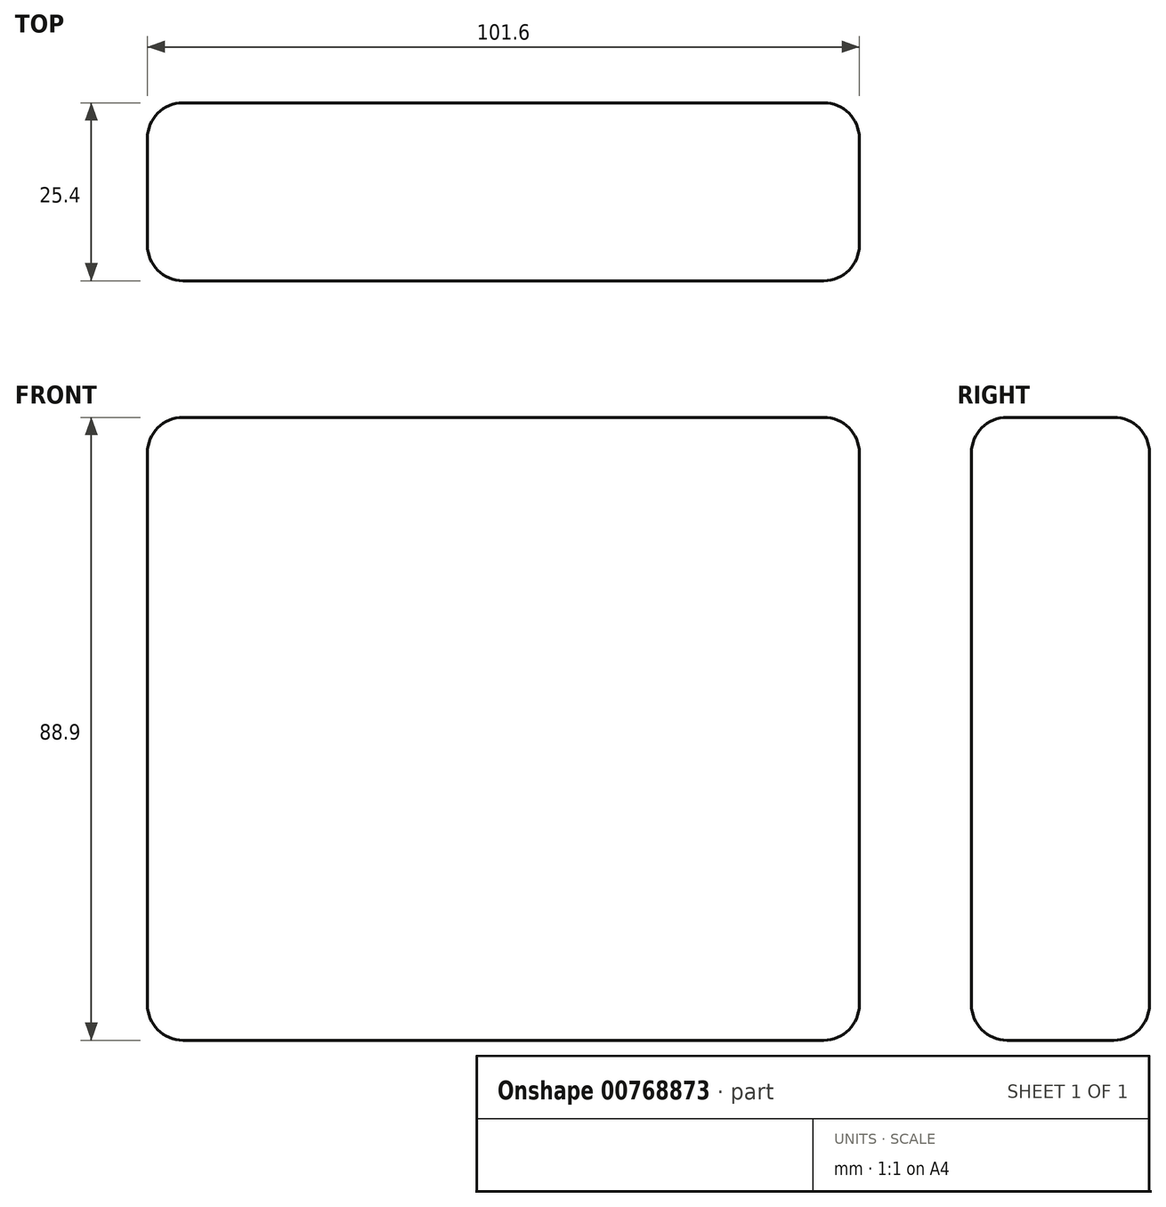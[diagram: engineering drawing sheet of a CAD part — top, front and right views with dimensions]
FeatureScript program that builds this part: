
annotation { "Feature Type Name" : "Feature", "Feature Type Description" : "" }
export const myFeature = defineFeature(function(context is Context, id is Id, definition is map)
    precondition{}
    {
        {
            var Q0;
            Q0=qCreatedBy(makeId("Front.planeOp"),FACE);
            var sketch = newSketch(context, id + "F0", { "sketchPlane" : qUnion([Q0])});
            skLineSegment(sketch, "E0.bottom", {"start": v(-50.8, -44.45) * mm, "end": v(50.8, -44.45) * mm});
            skLineSegment(sketch, "E0.top", {"start": v(-50.8, 44.45) * mm, "end": v(50.8, 44.45) * mm});
            skLineSegment(sketch, "E0.left", {"start": v(-50.8, -44.45) * mm, "end": v(-50.8, 44.45) * mm});
            skLineSegment(sketch, "E0.right", {"start": v(50.8, -44.45) * mm, "end": v(50.8, 44.45) * mm});
            skPoint(sketch, "E0.middle", {"position": v(0, 0) * mm});
            skSolve(sketch);
        }
        {
            var Q0;
            Q0 = qSketchRegion(id + "F0", true);
            extrude(context, id + "F1", {"entities" : qUnion([Q0]), "depth" : 25.4 * mm, "offsetDistance" : 25.4 * mm});
        }
        {
            var Q0;
            Q0=makeQuery(id+"F1.opExtrude","CAP_EDGE",EDGE,{"disambiguationData":[OSD([sQuery(id+"F0.wireOp",EDGE,"E0.top")])],"isStart":false});
            var Q1;
            Q1=makeQuery(id+"F1.opExtrude","CAP_EDGE",EDGE,{"disambiguationData":[OSD([sQuery(id+"F0.wireOp",EDGE,"E0.right")])],"isStart":false});
            var Q2;
            Q2=makeQuery(id+"F1.opExtrude","CAP_EDGE",EDGE,{"disambiguationData":[OSD([sQuery(id+"F0.wireOp",EDGE,"E0.bottom")])],"isStart":false});
            var Q3;
            Q3=makeQuery(id+"F1.opExtrude","CAP_EDGE",EDGE,{"disambiguationData":[OSD([sQuery(id+"F0.wireOp",EDGE,"E0.left")])],"isStart":false});
            var Q4;
            Q4=makeQuery(id+"F1.opExtrude","CAP_EDGE",EDGE,{"disambiguationData":[OSD([sQuery(id+"F0.wireOp",EDGE,"E0.top")])],"isStart":true});
            var Q5;
            Q5=makeQuery(id+"F1.opExtrude","SWEPT_EDGE",EDGE,{"disambiguationData":[OSD([sQuery(id+"F0.wireOp",EDGE,"E0.top"),sQuery(id+"F0.wireOp",EDGE,"E0.left")])]});
            var Q6;
            Q6=makeQuery(id+"F1.opExtrude","SWEPT_EDGE",EDGE,{"disambiguationData":[OSD([sQuery(id+"F0.wireOp",EDGE,"E0.top"),sQuery(id+"F0.wireOp",EDGE,"E0.right")])]});
            var Q7;
            Q7=makeQuery(id+"F1.opExtrude","CAP_EDGE",EDGE,{"disambiguationData":[OSD([sQuery(id+"F0.wireOp",EDGE,"E0.left")])],"isStart":true});
            var Q8;
            Q8=makeQuery(id+"F1.opExtrude","SWEPT_EDGE",EDGE,{"disambiguationData":[OSD([sQuery(id+"F0.wireOp",EDGE,"E0.bottom"),sQuery(id+"F0.wireOp",EDGE,"E0.left")])]});
            var Q9;
            Q9=makeQuery(id+"F1.opExtrude","CAP_EDGE",EDGE,{"disambiguationData":[OSD([sQuery(id+"F0.wireOp",EDGE,"E0.right")])],"isStart":true});
            var Q10;
            Q10=makeQuery(id+"F1.opExtrude","SWEPT_FACE",FACE,{"disambiguationData":[OSD([sQuery(id+"F0.wireOp",EDGE,"E0.right")])]});
            var Q11;
            Q11=makeQuery(id+"F1.opExtrude","CAP_EDGE",EDGE,{"disambiguationData":[OSD([sQuery(id+"F0.wireOp",EDGE,"E0.bottom")])],"isStart":true});
            fillet(context, id + "F2", {"entities" : qUnion([Q0, Q1, Q2, Q3, Q4, Q5, Q6, Q7, Q8, Q9, Q10, Q11]), "radius" : 5.08 * mm, "tangentPropagation" : true, "allowEdgeOverflow" : false});
        }
    });
